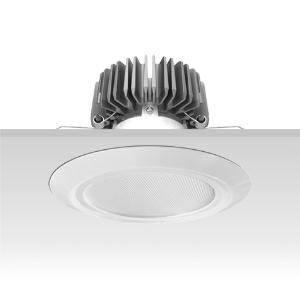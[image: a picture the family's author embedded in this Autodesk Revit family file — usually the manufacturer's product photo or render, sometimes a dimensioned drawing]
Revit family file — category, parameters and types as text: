
# Revit family: 3f_filippi_-_3f_reno_bianco_ampio_3f_filippi_-_30641_a01037_-_3f_reno_200_wh_4000-930_wide___vs_wh_9c2a
name_source: partatom
category: Lighting Fixtures
units: mm (PartAtom-declared; Revit-internal decimal feet)

## family parameters
Cut with Voids When Loaded = No
Host = Face
Light Source = No
Part Type = Normal
Room Calculation Point = No
Round Connector Dimension = Use Diameter
Shared = No

## types (1)
- 3F Filippi - 3F Reno Bianco Ampio (1 x LED, 2801 lm, 43 W, 3000 K)
    Apparent Load = 43 VA
    Approval mark = CE
    CIE Flux Codes = 75 94 99 100 100
    Color Rendering = 90
    Color Temperature = 3000 K
    Control Gear = Electronic ballast
    Default Elevation = 1800 mm
    Description = ILLUMINOTECHNICAL
Luminous efficiency 100% (DLOR 100%, ULOR 0%).
Initial luminous flux of the luminaire 2801 lm.
Direct symmetric wide distribution.
Installation Interdistance Transv.D = 1.16 x hu - Long.D = 1.14 x hu.
Tabular UGR (CIE 117 - 4H-8H; S=0.25H; 70/50/20): RUG 22.1 - 22.
Beam angle: 74° - 74°.
Luminous efficacy 65 lm/W.
Lifetime (L90/B10): 30000 h. (tq+25°C)
Lifetime (L85/B10): 50000 h. (tq+25°C)
Lifetime (L70/B10): 80000 h. (tq+25°C)
Sudden decreased luminous flux after 50000 hours: 0% (C0).
Photobiological safety in compliance with IEC/TR 62778: RG1 low risk, (IEC 62471).
In compliance with IEC/EN 62722-2-1 - IEC/EN 62717 standards.

SOURCE
Compact LED module 4000/930.
Energy efficiency class (UE 2019/2020 - UE 2019/2015): F.
CIE 13.3 Colour rendering index: CRI >90 (R9 >50%).
IES TM-30 Fidelity Index: Rf = 92 Rg = 101.
CCT nominal colour temperature 3000 K.
Colour initial tolerance (MacAdam): SDCM 3.
Zhaga Book 3 compliant.

MECHANICAL
Passive heat dissipator in die-casting aluminium, oversized, for optimum thermal management of the LED module.
Parabolic element with graduated/concentric rings in white polycarbonate.
Transparent external lens with glossy and satin differentiated surfaces, with a cooling and anti-insect system in methacrylate (PMMA).
Fastening spring clips in stainless steel.
Dimensions: diameter 226 mm, height 146 mm. Weight 1.8 kg.
IP44 protection degree for exposed part, IP20 for recessed part.
Mechanical strength to impacts IK06 (1 joule).
Glow-wire test resistance 650°C.

ELECTRICAL
Wiring on a separate unit.
Halogen Free electronic wiring 230V-50/60Hz, power factor 0.95, THD <25%, constant output current, SELV, class II, 1 driver.
Power of the luminaire 43 W.
ENEC - CE.
SAFE FLICKER: PstLM=<1 and SVM=<0.4 (IEC TR 61547-1 and IEC TR 63158), to ensure a more comfortable and safe light.
Luminaire compliant with EN 60598-2-22 for power supply from a centralised emergency system CPSS (Central Power Supply System), not incorporated in the luminaire - high risk areas excluded. The default power and flux are 100% in AC and 100% in DC.
Ambient temperature from 0°C to +25°C.
Temperature class T6 max 85°C.
Relative humidity UR: <85%.

INSTALLATION
Pull-up recessed fitting.
False ceiling carving: 200 mm.
All accessories dedicated to this product are available on the Catalog and on our website www.3F-Filippi.com.

ACCESSORIES
A01037 - Anti-glare microprismatic VS moulded glass, tempered, not flammable, locked and in line with the trim, in white polycarbonate.

APPLICATIONS
Environments: architectural, commercial, exhibition areas, transit areas, corridors, shops, display windows, service areas.
In false ceilings with narrow voids.

WARNING
Luminaire designed for disposal/recycling at end-of-life.
Replaceable (LED only) light source by a professional. Replaceable control gear by a professional.
    Height = 0 mm  [stored 0 ft]
    Lamp = 1 x LED
    Lamp Light Flux = 2801 lm
    Lamp Power = 43 W
    Lamp count = 1
    Length = 226 mm
    Lifetime = 50000 h
    Luminous efficacy = 65 lm/W
    Manufacturer = 3F Filippi
    ModVariant = No
    Model = 3F Filippi - 30641+A01037 - 3F Reno 200 WH 4000-930 WIDE + VS WH
    Mounting Place = Ceiling
    Mounting Type = Recessed
    Number of Poles = 1
    OnlyDefault = Yes
    Power Factor = 1
    Product Name = 3F Filippi - 3F Reno Bianco Ampio
    Product group = recessed luminaire
    ProductGroupID = 4
    Protection Class = Protection class II
    Protection Degree = IP 20
    RLX_Detail_Level = 1
    RLX_Emergency_Light_Flux = 0 lm
    RLX_Emergency_Type = 0
    RLX_Emergency_Type_DB = No
    RlxData = <blob elided: 93925 chars, md5=019800c6>
    Socket = socket
    Standby Power = 0 W
    System Light Flux = 2801 lm
    System Power = 43 W
    Type Comments = Product without accessories
    Type Image = 3ffilippi_3f_reno_200_wh_vs_smp.jpg
    URL = http://relux.com
    VarID = ---
    Voltage = 0 V
    Weight = 0.00 kg
    Width = 0 mm  [stored 0 ft]

note: [stored X ft] marks values corroborated as IEEE doubles in the binary element streams (Revit-internal decimal feet)

## geometry (parser evidence)
native form markers: Blend x4, Sweep x10
no freeform markers — native parametric forms only
